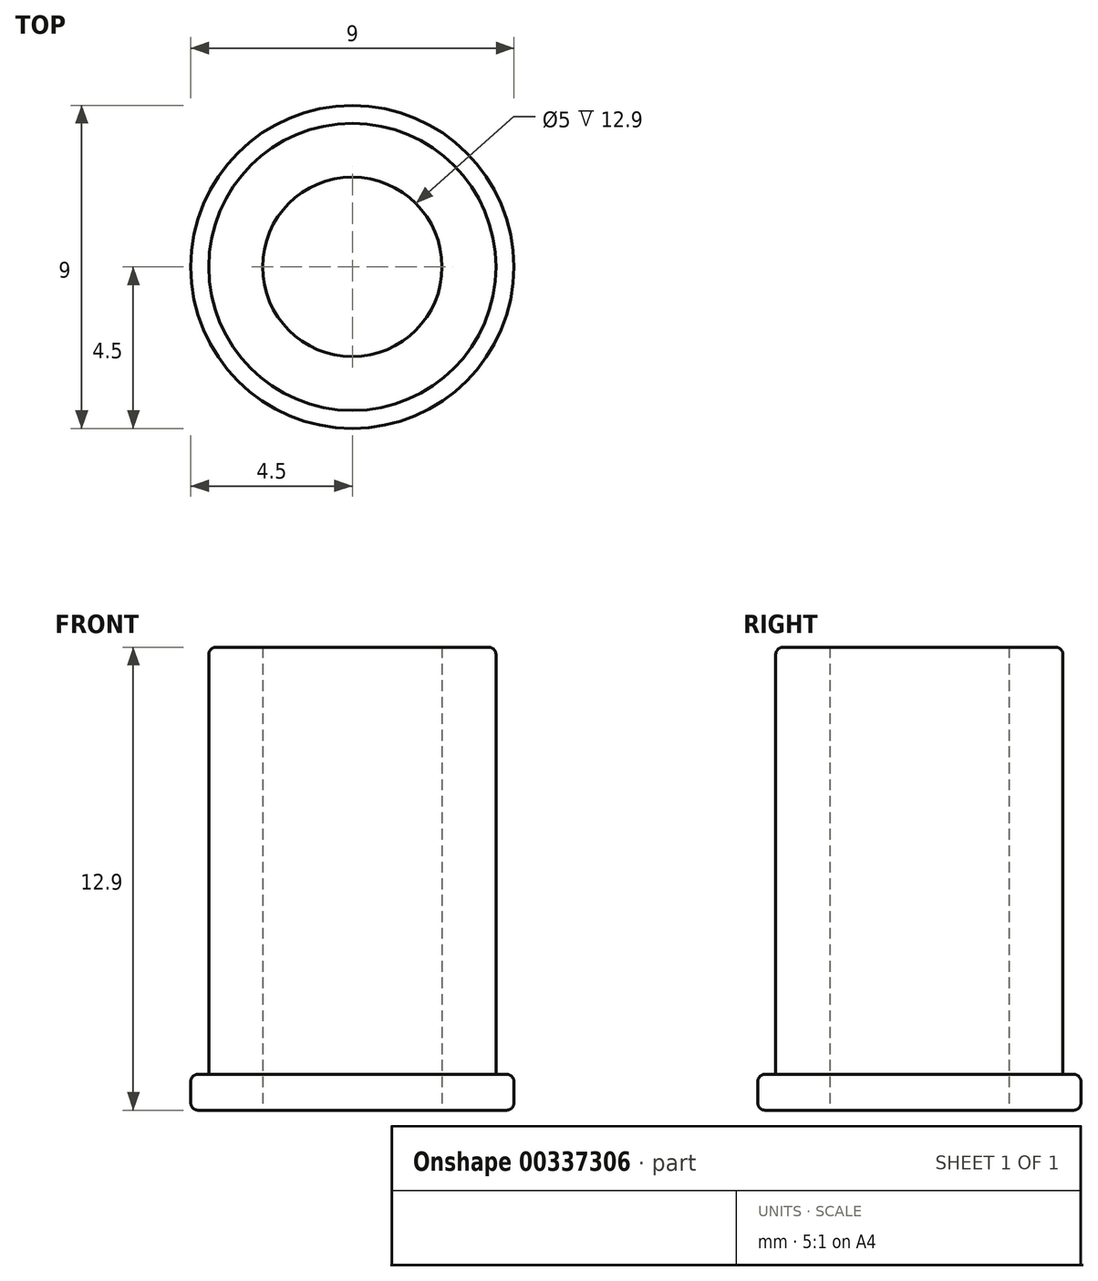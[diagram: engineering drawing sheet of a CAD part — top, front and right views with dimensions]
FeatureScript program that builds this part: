
annotation { "Feature Type Name" : "Feature", "Feature Type Description" : "" }
export const myFeature = defineFeature(function(context is Context, id is Id, definition is map)
    precondition{}
    {
        {
            var Q0;
            Q0=qCreatedBy(makeId("Top.planeOp"),FACE);
            var sketch = newSketch(context, id + "F0", { "sketchPlane" : qUnion([Q0])});
            skCircle(sketch, "E0", {"center": v(0, 0) * mm, "radius": 4.5 * mm});
            skCircle(sketch, "E1", {"center": v(0, 0) * mm, "radius": 4 * mm});
            skCircle(sketch, "E2", {"center": v(0, 0) * mm, "radius": 2.5 * mm});
            skSolve(sketch);
        }
        {
            var Q0;
            Q0=qSketchRegion(id+"F0",true);
            extrude(context, id + "F1", {"entities" : qUnion([Q0]), "depth" : 1 * mm});
        }
        {
            var Q0;
            Q0=makeQuery(id+"F0.imprint","IMPRINT",FACE,{"disambiguationData":[TD([[makeQuery(id+"F0.imprint","IMPRINT",EDGE,{"derivedFrom":sQuery(id+"F0.wireOp",EDGE,"E1")}),1.0]])]});
            extrude(context, id + "F2", {"entities" : qUnion([Q0]), "operationType" : NewBodyOperationType.ADD, "depth" : 12.9 * mm});
        }
        {
            var Q0;
            Q0=makeQuery(id+"F1.opExtrude","CAP_EDGE",EDGE,{"disambiguationData":[OSD([sQuery(id+"F0.wireOp",EDGE,"E0")])],"isStart":true});
            fillet(context, id + "F3", {"entities" : qUnion([Q0]), "radius" : 0.2 * mm, "tangentPropagation" : true, "allowEdgeOverflow" : false});
        }
        {
            var Q0;
            Q0=makeQuery(id+"F1.opExtrude","CAP_EDGE",EDGE,{"disambiguationData":[OSD([sQuery(id+"F0.wireOp",EDGE,"E0")])],"isStart":false});
            fillet(context, id + "F4", {"entities" : qUnion([Q0]), "radius" : 0.2 * mm, "tangentPropagation" : true, "allowEdgeOverflow" : false});
        }
        {
            var Q0;
            Q0=makeQuery(id+"F2.opExtrude","CAP_EDGE",EDGE,{"disambiguationData":[OSD([sQuery(id+"F0.wireOp",EDGE,"E1")])],"isStart":false});
            fillet(context, id + "F5", {"entities" : qUnion([Q0]), "radius" : 0.2 * mm, "tangentPropagation" : true, "allowEdgeOverflow" : false});
        }
    });
